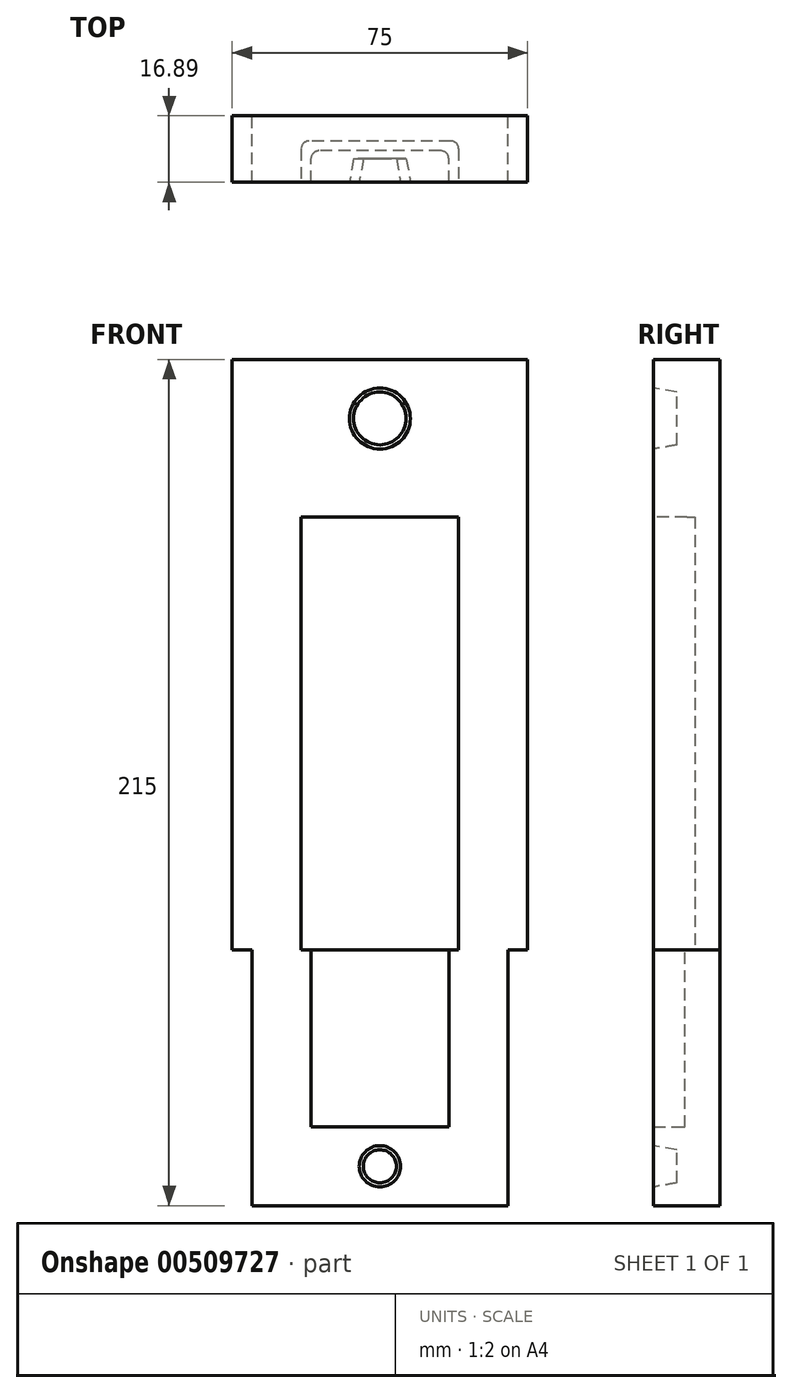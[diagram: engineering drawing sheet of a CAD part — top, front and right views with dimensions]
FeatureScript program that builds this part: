
annotation { "Feature Type Name" : "Feature", "Feature Type Description" : "" }
export const myFeature = defineFeature(function(context is Context, id is Id, definition is map)
    precondition{}
    {
        {
            var Q0;
            Q0=qCreatedBy(makeId("Top.planeOp"),FACE);
            var sketch = newSketch(context, id + "F0", { "sketchPlane" : qUnion([Q0])});
            skLineSegment(sketch, "E0.bottom", {"start": v(32.5, -23) * mm, "end": v(-32.5, -23) * mm});
            skLineSegment(sketch, "E0.top", {"start": v(32.5, 23) * mm, "end": v(-32.5, 23) * mm});
            skLineSegment(sketch, "E0.left", {"start": v(32.5, -23) * mm, "end": v(32.5, 23) * mm});
            skLineSegment(sketch, "E0.right", {"start": v(-32.5, -23) * mm, "end": v(-32.5, 23) * mm});
            skPoint(sketch, "E0.middle", {"position": v(0, 0) * mm});
            skSolve(sketch);
        }
        {
            var Q0;
            Q0=qSketchRegion(id+"F0",true);
            extrude(context, id + "F1", {"entities" : qUnion([Q0]), "depth" : 65 * mm});
        }
        {
            var Q0;
            Q0=makeQuery(id+"F1.opExtrude","CAP_FACE",FACE,{"disambiguationData":[OSD([sQuery(id+"F0.wireOp",EDGE,"E0.bottom"),sQuery(id+"F0.wireOp",EDGE,"E0.top"),sQuery(id+"F0.wireOp",EDGE,"E0.left"),sQuery(id+"F0.wireOp",EDGE,"E0.right")])],"isStart":false});
            var sketch = newSketch(context, id + "F2", { "sketchPlane" : qUnion([Q0])});
            skLineSegment(sketch, "E1.bottom", {"start": v(17.5, -8) * mm, "end": v(-17.5, -8) * mm});
            skLineSegment(sketch, "E1.top", {"start": v(17.5, 8) * mm, "end": v(-17.5, 8) * mm});
            skLineSegment(sketch, "E1.left", {"start": v(17.5, -8) * mm, "end": v(17.5, 8) * mm});
            skLineSegment(sketch, "E1.right", {"start": v(-17.5, -8) * mm, "end": v(-17.5, 8) * mm});
            skPoint(sketch, "E1.middle", {"position": v(0, 0) * mm});
            skSolve(sketch);
        }
        {
            var Q0;
            Q0=qSketchRegion(id+"F2",true);
            extrude(context, id + "F3", {"entities" : qUnion([Q0]), "operationType" : NewBodyOperationType.REMOVE, "oppositeDirection" : true, "depth" : 45 * mm});
        }
        {
            var Q0;
            Q0=makeQuery(id+"F3.boolean.opBoolean","COPY",EDGE,{"derivedFrom":makeQuery(id+"F3.opExtrude","SWEPT_EDGE",EDGE,{"disambiguationData":[OSD([sQuery(id+"F2.wireOp",EDGE,"E1.bottom"),sQuery(id+"F2.wireOp",EDGE,"E1.right")])]})});
            var Q1;
            Q1=makeQuery(id+"F3.boolean.opBoolean","COPY",EDGE,{"derivedFrom":makeQuery(id+"F3.opExtrude","SWEPT_EDGE",EDGE,{"disambiguationData":[OSD([sQuery(id+"F2.wireOp",EDGE,"E1.top"),sQuery(id+"F2.wireOp",EDGE,"E1.right")])]})});
            var Q2;
            Q2=makeQuery(id+"F3.boolean.opBoolean","COPY",EDGE,{"derivedFrom":makeQuery(id+"F3.opExtrude","SWEPT_EDGE",EDGE,{"disambiguationData":[OSD([sQuery(id+"F2.wireOp",EDGE,"E1.bottom"),sQuery(id+"F2.wireOp",EDGE,"E1.left")])]})});
            var Q3;
            Q3=makeQuery(id+"F3.boolean.opBoolean","COPY",EDGE,{"derivedFrom":makeQuery(id+"F3.opExtrude","SWEPT_EDGE",EDGE,{"disambiguationData":[OSD([sQuery(id+"F2.wireOp",EDGE,"E1.top"),sQuery(id+"F2.wireOp",EDGE,"E1.left")])]})});
            fillet(context, id + "F4", {"entities" : qUnion([Q0, Q1, Q2, Q3]), "radius" : 2 * mm, "tangentPropagation" : true, "allowEdgeOverflow" : false});
        }
        {
            var Q0;
            Q0=makeQuery(id+"F1.opExtrude","CAP_FACE",FACE,{"disambiguationData":[OSD([sQuery(id+"F0.wireOp",EDGE,"E0.bottom"),sQuery(id+"F0.wireOp",EDGE,"E0.top"),sQuery(id+"F0.wireOp",EDGE,"E0.left"),sQuery(id+"F0.wireOp",EDGE,"E0.right")])],"isStart":false});
            var sketch = newSketch(context, id + "F5", { "sketchPlane" : qUnion([Q0])});
            skLineSegment(sketch, "E2.bottom", {"start": v(37.5, -26.9) * mm, "end": v(-37.5, -26.9) * mm});
            skLineSegment(sketch, "E2.top", {"start": v(37.5, 26.9) * mm, "end": v(-37.5, 26.9) * mm});
            skLineSegment(sketch, "E2.left", {"start": v(37.5, -26.9) * mm, "end": v(37.5, 26.9) * mm});
            skLineSegment(sketch, "E2.right", {"start": v(-37.5, -26.9) * mm, "end": v(-37.5, 26.9) * mm});
            skPoint(sketch, "E2.middle", {"position": v(0, 0) * mm});
            skSolve(sketch);
        }
        {
            var Q0;
            Q0=qSketchRegion(id+"F5",true);
            extrude(context, id + "F6", {"entities" : qUnion([Q0]), "operationType" : NewBodyOperationType.ADD, "depth" : 150 * mm});
        }
        {
            var Q0;
            {var subQ0=sQuery(id+"F5.wireOp",EDGE,"E2.right");var subQ1=sQuery(id+"F5.wireOp",EDGE,"E2.left");var subQ2=sQuery(id+"F5.wireOp",EDGE,"E2.bottom");var subQ3=sQuery(id+"F5.wireOp",EDGE,"E2.top");Q0=makeQuery(id+"F6.boolean.opBoolean","SPLIT",FACE,{"disambiguationData":[TD([makeQuery(id+"F1.opExtrude","SWEPT_FACE",FACE,{"disambiguationData":[OSD([sQuery(id+"F0.wireOp",EDGE,"E0.bottom")])]})])],"derivedFrom":makeQuery(id+"F6.opExtrude","CAP_FACE",FACE,{"disambiguationData":[OSD([subQ2,subQ3,subQ1,subQ0])],"isStart":true})});}
            var sketch = newSketch(context, id + "F7", { "sketchPlane" : qUnion([Q0])});
            skLineSegment(sketch, "E3.bottom", {"start": v(20, -10.5) * mm, "end": v(-20, -10.5) * mm});
            skLineSegment(sketch, "E3.top", {"start": v(20, 10.5) * mm, "end": v(-20, 10.5) * mm});
            skLineSegment(sketch, "E3.left", {"start": v(20, -10.5) * mm, "end": v(20, 10.5) * mm});
            skLineSegment(sketch, "E3.right", {"start": v(-20, -10.5) * mm, "end": v(-20, 10.5) * mm});
            skPoint(sketch, "E3.middle", {"position": v(0, 0) * mm});
            skSolve(sketch);
        }
        {
            var Q0;
            Q0=qSketchRegion(id+"F7",true);
            extrude(context, id + "F8", {"entities" : qUnion([Q0]), "operationType" : NewBodyOperationType.REMOVE, "oppositeDirection" : true, "depth" : 110 * mm});
        }
        {
            var Q0;
            Q0=makeQuery(id+"F8.boolean.opBoolean","COPY",EDGE,{"derivedFrom":makeQuery(id+"F8.opExtrude","SWEPT_EDGE",EDGE,{"disambiguationData":[OSD([sQuery(id+"F7.wireOp",EDGE,"E3.top"),sQuery(id+"F7.wireOp",EDGE,"E3.right")])]})});
            fillet(context, id + "F9", {"entities" : qUnion([Q0]), "radius" : 2 * mm, "tangentPropagation" : true, "allowEdgeOverflow" : false});
        }
        {
            var Q0;
            Q0=makeQuery(id+"F8.boolean.opBoolean","COPY",EDGE,{"derivedFrom":makeQuery(id+"F8.opExtrude","SWEPT_EDGE",EDGE,{"disambiguationData":[OSD([sQuery(id+"F7.wireOp",EDGE,"E3.bottom"),sQuery(id+"F7.wireOp",EDGE,"E3.right")])]})});
            fillet(context, id + "F10", {"entities" : qUnion([Q0]), "radius" : 2 * mm, "tangentPropagation" : true, "allowEdgeOverflow" : false});
        }
        {
            var Q0;
            Q0=makeQuery(id+"F8.boolean.opBoolean","COPY",EDGE,{"derivedFrom":makeQuery(id+"F8.opExtrude","SWEPT_EDGE",EDGE,{"disambiguationData":[OSD([sQuery(id+"F7.wireOp",EDGE,"E3.top"),sQuery(id+"F7.wireOp",EDGE,"E3.left")])]})});
            var Q1;
            Q1=makeQuery(id+"F8.boolean.opBoolean","COPY",EDGE,{"derivedFrom":makeQuery(id+"F8.opExtrude","SWEPT_EDGE",EDGE,{"disambiguationData":[OSD([sQuery(id+"F7.wireOp",EDGE,"E3.bottom"),sQuery(id+"F7.wireOp",EDGE,"E3.left")])]})});
            fillet(context, id + "F11", {"entities" : qUnion([Q0, Q1]), "radius" : 2 * mm, "tangentPropagation" : true, "allowEdgeOverflow" : false});
        }
        {
            var Q0;
            Q0=qCreatedBy(makeId("Front.planeOp"),FACE);
            var sketch = newSketch(context, id + "F12", { "sketchPlane" : qUnion([Q0])});
            skLineSegment(sketch, "E4.bottom", {"start": v(75.37, -45.34) * mm, "end": v(-75.37, -45.34) * mm});
            skLineSegment(sketch, "E4.top", {"start": v(75.37, 298.39) * mm, "end": v(-75.37, 298.39) * mm});
            skLineSegment(sketch, "E4.left", {"start": v(75.37, -45.34) * mm, "end": v(75.37, 298.39) * mm});
            skLineSegment(sketch, "E4.right", {"start": v(-75.37, -45.34) * mm, "end": v(-75.37, 298.39) * mm});
            skPoint(sketch, "E4.middle", {"position": v(0, 126.53) * mm});
            skSolve(sketch);
        }
        {
            var Q0;
            Q0=makeQuery(id+"F12.imprint","IMPRINT",FACE,{"disambiguationData":[TD([[makeQuery(id+"F12.imprint","IMPRINT",EDGE,{"derivedFrom":sQuery(id+"F12.wireOp",EDGE,"E4.bottom")}),-1.0]])]});
            var Q1;
            Q1=makeQuery(id+"F6.opExtrude","SWEPT_FACE",FACE,{"disambiguationData":[OSD([sQuery(id+"F5.wireOp",EDGE,"E2.bottom")])]});
            var Q2;
            Q2=makeQuery(id+"F1.opExtrude","SWEPT_FACE",FACE,{"disambiguationData":[OSD([sQuery(id+"F0.wireOp",EDGE,"E0.bottom")])]});
            extrude(context, id + "F13", {"entities" : qUnion([Q0, Q1, Q2]), "operationType" : NewBodyOperationType.REMOVE, "endBound" : BoundingType.THROUGH_ALL, "depth" : 25 * mm});
        }
        {
            var Q0;
            Q0=makeQuery(id+"F13.boolean.opBoolean","COPY",FACE,{"derivedFrom":makeQuery(id+"F13.opExtrude","CAP_FACE",FACE,{"disambiguationData":[OSD([sQuery(id+"F12.wireOp",EDGE,"E4.bottom"),sQuery(id+"F12.wireOp",EDGE,"E4.top"),sQuery(id+"F12.wireOp",EDGE,"E4.left"),sQuery(id+"F12.wireOp",EDGE,"E4.right")])],"isStart":true})});
            var sketch = newSketch(context, id + "F14", { "sketchPlane" : qUnion([Q0])});
            skCircle(sketch, "E5", {"center": v(0, 200) * mm, "radius": 7.75 * mm});
            skPoint(sketch, "E5.centerSnap0", {"position": v(0, 215) * mm});
            skCircle(sketch, "E6", {"center": v(0, 10) * mm, "radius": 5.25 * mm});
            skSolve(sketch);
        }
        {
            var Q0;
            Q0=makeQuery(id+"F14.imprint","IMPRINT",FACE,{"disambiguationData":[TD([[makeQuery(id+"F14.imprint","IMPRINT",EDGE,{"derivedFrom":sQuery(id+"F14.wireOp",EDGE,"E5")}),1.0]])]});
            var Q1;
            Q1=makeQuery(id+"F14.imprint","IMPRINT",FACE,{"disambiguationData":[TD([[makeQuery(id+"F14.imprint","IMPRINT",EDGE,{"derivedFrom":sQuery(id+"F14.wireOp",EDGE,"E6")}),1.0]])]});
            extrude(context, id + "F15", {"entities" : qUnion([Q0, Q1]), "operationType" : NewBodyOperationType.REMOVE, "oppositeDirection" : true, "depth" : 6 * mm, "hasDraft" : true, "draftAngle" : 10 * degree, "draftPullDirection" : true});
        }
        {
            var Q0;
            Q0=makeQuery(id+"F6.opExtrude","SWEPT_FACE",FACE,{"disambiguationData":[OSD([sQuery(id+"F5.wireOp",EDGE,"E2.top")])]});
            var sketch = newSketch(context, id + "F16", { "sketchPlane" : qUnion([Q0])});
            skLineSegment(sketch, "E7.bottom", {"start": v(-53.3, 224.36) * mm, "end": v(89.86, 224.36) * mm});
            skLineSegment(sketch, "E7.top", {"start": v(-53.3, -43.27) * mm, "end": v(89.86, -43.27) * mm});
            skLineSegment(sketch, "E7.left", {"start": v(-53.3, 224.36) * mm, "end": v(-53.3, -43.27) * mm});
            skLineSegment(sketch, "E7.right", {"start": v(89.86, 224.36) * mm, "end": v(89.86, -43.27) * mm});
            skSolve(sketch);
        }
        {
            var Q0;
            Q0 = qSketchRegion(id + "F16", true);
            extrude(context, id + "F17", {"entities" : qUnion([Q0]), "operationType" : NewBodyOperationType.REMOVE, "oppositeDirection" : true, "depth" : 10 * mm});
        }
    });
